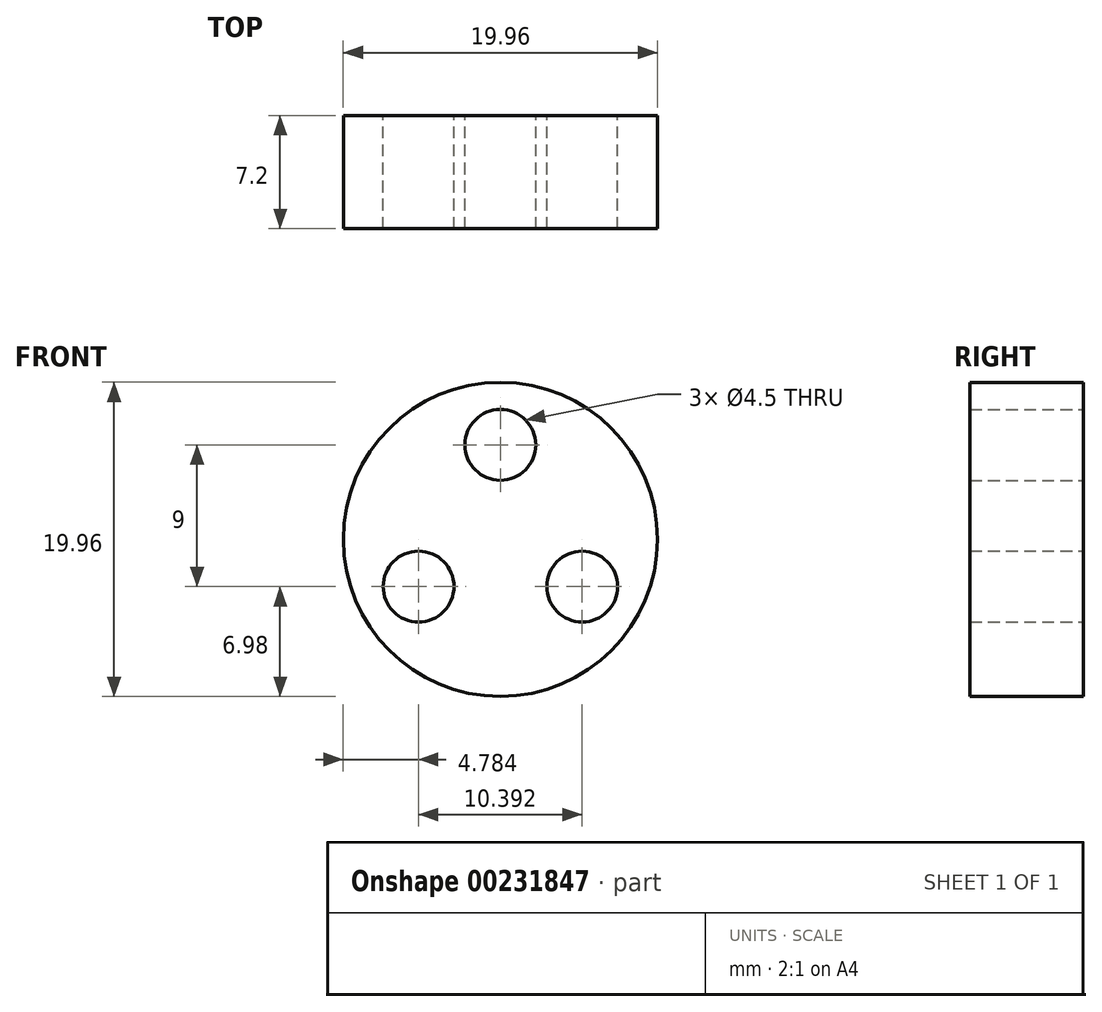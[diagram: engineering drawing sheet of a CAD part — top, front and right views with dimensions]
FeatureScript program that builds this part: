
annotation { "Feature Type Name" : "Feature", "Feature Type Description" : "" }
export const myFeature = defineFeature(function(context is Context, id is Id, definition is map)
    precondition{}
    {
        {
            var Q0;
            Q0=qCreatedBy(makeId("Right.planeOp"),FACE);
            var sketch = newSketch(context, id + "F0", { "sketchPlane" : qUnion([Q0])});
            skLineSegment(sketch, "E0.bottom", {"start": v(-7.2, 9.97) * mm, "end": v(0, 9.97) * mm});
            skLineSegment(sketch, "E0.left", {"start": v(-7.2, 9.97) * mm, "end": v(-7.2, 0) * mm});
            skLineSegment(sketch, "E0.right", {"start": v(0, 9.97) * mm, "end": v(0, 0) * mm});
            skPoint(sketch, "E0.middle", {"position": v(0, 0) * mm});
            skLineSegment(sketch, "E1", {"start": v(-7.2, 0) * mm, "end": v(0, 0) * mm});
            skSolve(sketch);
        }
        {
            var Q0;
            Q0=makeQuery(id+"F0.imprint","IMPRINT",FACE,{"disambiguationData":[TD([[makeQuery(id+"F0.imprint","IMPRINT",EDGE,{"derivedFrom":sQuery(id+"F0.wireOp",EDGE,"E0.bottom")}),-1.0]])]});
            var Q1;
            Q1=sQuery(id+"F0.wireOp",EDGE,"E1");
            revolve(context, id + "F1", {"entities" : qUnion([Q0]), "axis" : qUnion([Q1]), "revolveType" : RevolveType.FULL});
        }
        {
            var Q0;
            Q0=qCreatedBy(makeId("Front.planeOp"),FACE);
            var sketch = newSketch(context, id + "F2", { "sketchPlane" : qUnion([Q0])});
            skCircle(sketch, "E2", {"center": v(0, 0) * mm, "radius": 6 * mm});
            skPoint(sketch, "E3", {"position": v(0, 6) * mm});
            skPoint(sketch, "E4", {"position": v(-5.2, -3) * mm});
            skPoint(sketch, "E5", {"position": v(5.2, -3) * mm});
            skLineSegment(sketch, "E6", {"start": v(-5.2, -3) * mm, "end": v(0, 0) * mm});
            skLineSegment(sketch, "E7", {"start": v(5.2, -3) * mm, "end": v(0, 0) * mm});
            skLineSegment(sketch, "E8", {"start": v(0, 0) * mm, "end": v(0, 6) * mm});
            skSolve(sketch);
        }
        {
            var Q0;
            Q0=sQuery(id+"F2.wireOp",VERTEX,"E3");
            var Q1;
            Q1=sQuery(id+"F2.wireOp",VERTEX,"E4");
            var Q2;
            Q2=sQuery(id+"F2.wireOp",VERTEX,"E5");
            var Q3;
            Q3=makeQuery(id+"F1.opRevolve","SWEPT_BODY",BODY,{"disambiguationData":[OSD([sQuery(id+"F0.wireOp",EDGE,"E0.bottom"),sQuery(id+"F0.wireOp",EDGE,"E0.left"),sQuery(id+"F0.wireOp",EDGE,"E0.right"),sQuery(id+"F0.wireOp",EDGE,"E1")])]});
            hole(context, id + "F3", {"style" : HoleStyle.SIMPLE, "endStyle" : HoleEndStyle.THROUGH, "oppositeDirection" : true, "holeDiameter" : 4.5 * mm, "startFromSketch" : true, "locations" : qUnion([Q0, Q1, Q2]), "scope" : qUnion([Q3]), "isTappedThrough" : true});
        }
    });
